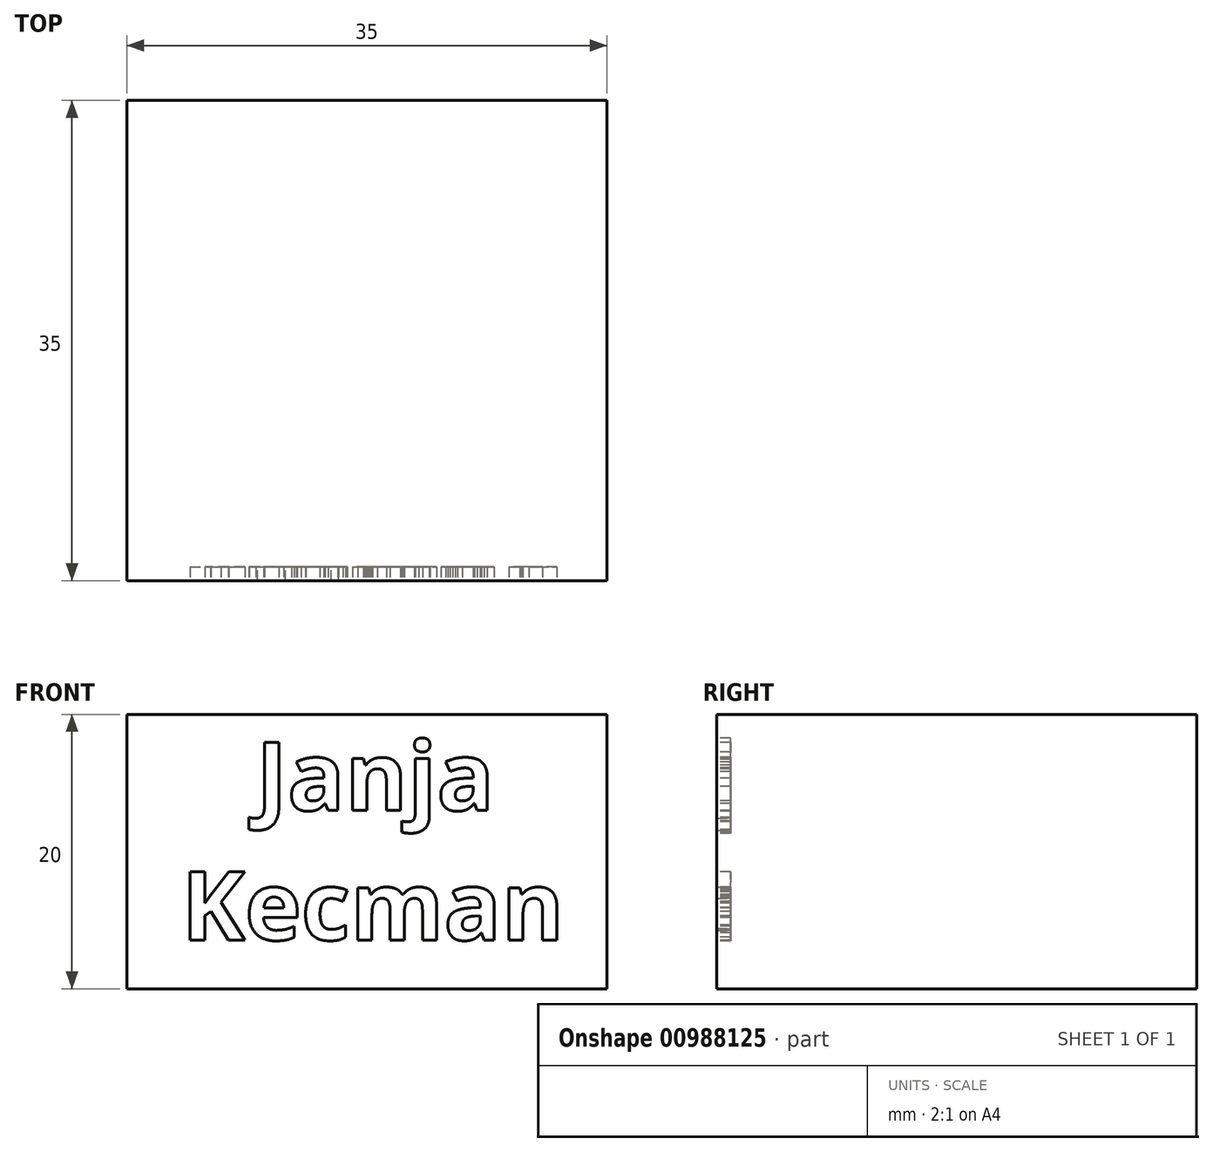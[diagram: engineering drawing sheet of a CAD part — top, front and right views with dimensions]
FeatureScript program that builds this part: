
annotation { "Feature Type Name" : "Feature", "Feature Type Description" : "" }
export const myFeature = defineFeature(function(context is Context, id is Id, definition is map)
    precondition{}
    {
        {
            var Q0;
            Q0=qCreatedBy(makeId("Top.planeOp"),FACE);
            var sketch = newSketch(context, id + "F0", { "sketchPlane" : qUnion([Q0])});
            skLineSegment(sketch, "E0.bottom", {"start": v(0, 0) * mm, "end": v(35, 0) * mm});
            skLineSegment(sketch, "E0.top", {"start": v(0, 35) * mm, "end": v(35, 35) * mm});
            skLineSegment(sketch, "E0.left", {"start": v(0, 0) * mm, "end": v(0, 35) * mm});
            skLineSegment(sketch, "E0.right", {"start": v(35, 0) * mm, "end": v(35, 35) * mm});
            skSolve(sketch);
        }
        {
            var Q0;
            Q0 = qSketchRegion(id + "F0", true);
            extrude(context, id + "F1", {"entities" : qUnion([Q0]), "depth" : 20 * mm, "offsetDistance" : 25 * mm});
        }
        {
            var Q0;
            Q0=makeQuery(id+"F1.opExtrude","SWEPT_FACE",FACE,{"disambiguationData":[OSD([sQuery(id+"F0.wireOp",EDGE,"E0.bottom")])]});
            var sketch = newSketch(context, id + "F2", { "sketchPlane" : qUnion([Q0])});
            skText(sketch, "E1", { "text": "   Janja\nKecman", "fontName": "OpenSans-Bold.ttf"});
            const initialGuessF2  = {"E1": [0.004, 0.013, 1, 0, 0.005]};
            skSetInitialGuess(sketch, initialGuessF2);
            skSolve(sketch);
        }
        {
            var Q0;
            Q0 = qSketchRegion(id + "F2", true);
            extrude(context, id + "F3", {"entities" : qUnion([Q0]), "operationType" : NewBodyOperationType.REMOVE, "oppositeDirection" : true, "depth" : 1 * mm, "offsetDistance" : 25 * mm});
        }
    });
